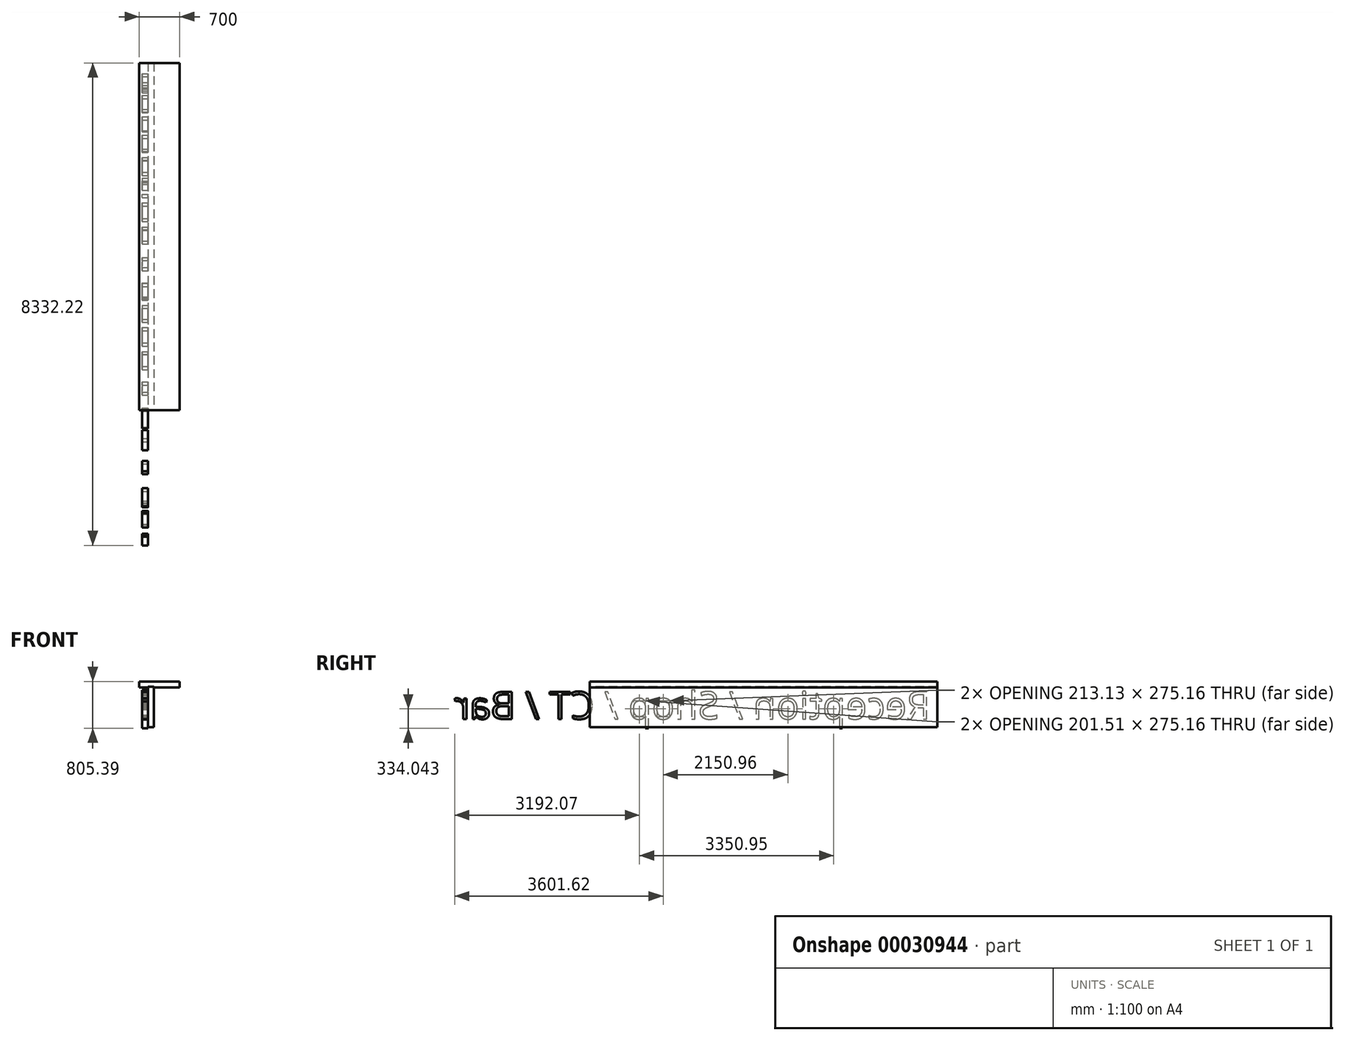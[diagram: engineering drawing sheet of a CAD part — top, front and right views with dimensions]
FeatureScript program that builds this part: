
annotation { "Feature Type Name" : "Feature", "Feature Type Description" : "" }
export const myFeature = defineFeature(function(context is Context, id is Id, definition is map)
    precondition{}
    {
        {
            var Q0;
            Q0=qCreatedBy(makeId("Front.planeOp"),FACE);
            var sketch = newSketch(context, id + "F0", { "sketchPlane" : qUnion([Q0])});
            skLineSegment(sketch, "E0.rect.bottom", {"start": v(-50, 350) * mm, "end": v(50, 350) * mm});
            skLineSegment(sketch, "E0.rect.top", {"start": v(-50, -350) * mm, "end": v(50, -350) * mm});
            skLineSegment(sketch, "E0.rect.left", {"start": v(-50, 350) * mm, "end": v(-50, -350) * mm});
            skLineSegment(sketch, "E0.rect.right", {"start": v(50, 350) * mm, "end": v(50, -350) * mm});
            skPoint(sketch, "E0.rect.middle", {"position": v(0, 0) * mm});
            skSolve(sketch);
        }
        {
            var Q0;
            Q0 = qSketchRegion(id + "F0", true);
            extrude(context, id + "F1", {"entities" : qUnion([Q0]), "depth" : 6000 * mm});
        }
        {
            var Q0;
            Q0=makeQuery(id+"F1.opExtrude","CAP_FACE",FACE,{"disambiguationData":[OSD([sQuery(id+"F0.wireOp",EDGE,"E0.rect.bottom"),sQuery(id+"F0.wireOp",EDGE,"E0.rect.top"),sQuery(id+"F0.wireOp",EDGE,"E0.rect.left"),sQuery(id+"F0.wireOp",EDGE,"E0.rect.right")])],"isStart":false});
            var sketch = newSketch(context, id + "F2", { "sketchPlane" : qUnion([Q0])});
            skLineSegment(sketch, "E1.bottom", {"start": v(-203.46, 338.71) * mm, "end": v(496.54, 338.71) * mm});
            skLineSegment(sketch, "E1.top", {"start": v(-203.46, 438.71) * mm, "end": v(496.54, 438.71) * mm});
            skLineSegment(sketch, "E1.left", {"start": v(-203.46, 338.71) * mm, "end": v(-203.46, 438.71) * mm});
            skLineSegment(sketch, "E1.right", {"start": v(496.54, 338.71) * mm, "end": v(496.54, 438.71) * mm});
            skLineSegment(sketch, "E2.bottom", {"start": v(496.54, 338.71) * mm, "end": v(496.54, 349.24) * mm});
            skSolve(sketch);
        }
        {
            var Q0;
            Q0=makeQuery(id+"F2.imprint","IMPRINT",FACE,{"disambiguationData":[TD([[makeQuery(id+"F2.imprint","IMPRINT",EDGE,{"derivedFrom":sQuery(id+"F2.wireOp",EDGE,"E1.top")}),-1.0]])]});
            extrude(context, id + "F3", {"entities" : qUnion([Q0]), "oppositeDirection" : true, "depth" : 6000 * mm});
        }
        {
            var Q0;
            Q0=makeQuery(id+"F1.opExtrude","SWEPT_FACE",FACE,{"disambiguationData":[OSD([sQuery(id+"F0.wireOp",EDGE,"E0.rect.left")])]});
            var sketch = newSketch(context, id + "F4", { "sketchPlane" : qUnion([Q0])});
            skText(sketch, "E3", { "text": "Reception / Shop / CT / Bar", "fontName": "OpenSans-Regular.ttf"});
            const initialGuessF4  = {"E3": [0.11938, -0.20848, 1, 0, 0.47399]};
            skSetInitialGuess(sketch, initialGuessF4);
            skSolve(sketch);
        }
        {
            var Q0;
            Q0 = qSketchRegion(id + "F4", true);
            extrude(context, id + "F5", {"entities" : qUnion([Q0]), "depth" : 100 * mm});
        }
    });
